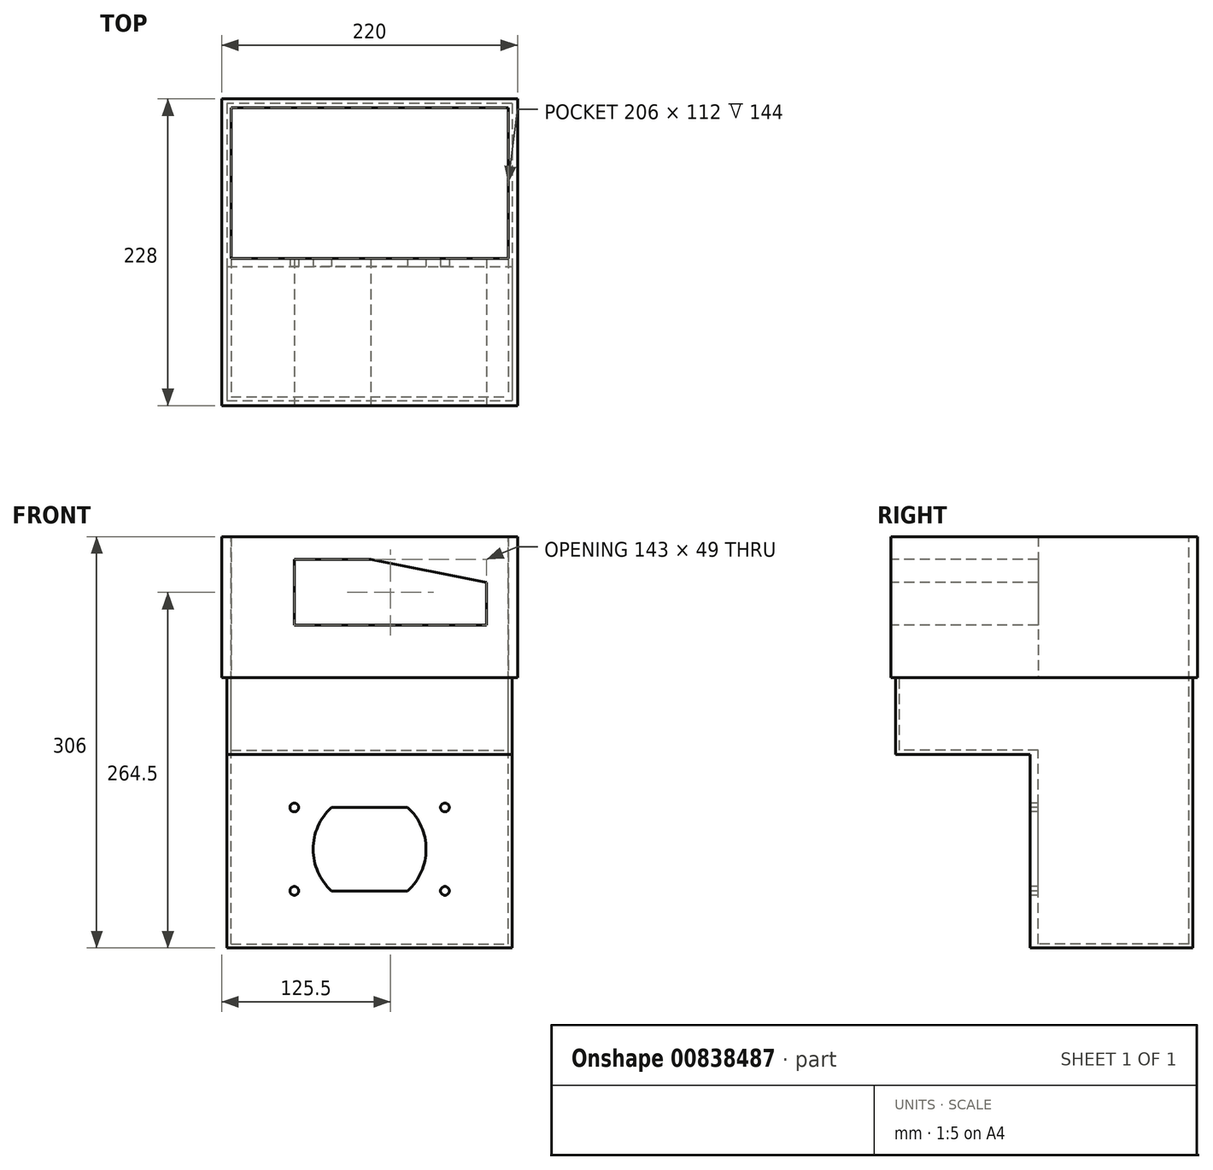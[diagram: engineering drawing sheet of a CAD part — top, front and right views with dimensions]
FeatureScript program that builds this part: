
annotation { "Feature Type Name" : "Feature", "Feature Type Description" : "" }
export const myFeature = defineFeature(function(context is Context, id is Id, definition is map)
    precondition{}
    {
        {
            var Q0;
            Q0=qCreatedBy(makeId("Top.planeOp"),FACE);
            var sketch = newSketch(context, id + "F0", { "sketchPlane" : qUnion([Q0])});
            skLineSegment(sketch, "E0.bottom", {"start": v(106, 110.5) * mm, "end": v(-106, 110.5) * mm});
            skLineSegment(sketch, "E0.top", {"start": v(106, -110.5) * mm, "end": v(-106, -110.5) * mm});
            skLineSegment(sketch, "E0.left", {"start": v(106, 110.5) * mm, "end": v(106, -110.5) * mm});
            skLineSegment(sketch, "E0.right", {"start": v(-106, 110.5) * mm, "end": v(-106, -110.5) * mm});
            skPoint(sketch, "E0.middle", {"position": v(0, 0) * mm});
            skSolve(sketch);
        }
        {
            var Q0;
            Q0=makeQuery(id+"F0.imprint","IMPRINT",FACE,{"disambiguationData":[TD([[makeQuery(id+"F0.imprint","IMPRINT",EDGE,{"derivedFrom":sQuery(id+"F0.wireOp",EDGE,"E0.bottom")}),1.0]])]});
            extrude(context, id + "F1", {"entities" : qUnion([Q0]), "depth" : 201 * mm, "offsetDistance" : 25 * mm});
        }
        {
            var Q0;
            Q0=makeQuery(id+"F1.opExtrude","CAP_FACE",FACE,{"disambiguationData":[OSD([sQuery(id+"F0.wireOp",EDGE,"E0.bottom"),sQuery(id+"F0.wireOp",EDGE,"E0.top"),sQuery(id+"F0.wireOp",EDGE,"E0.left"),sQuery(id+"F0.wireOp",EDGE,"E0.right")])],"isStart":false});
            var sketch = newSketch(context, id + "F2", { "sketchPlane" : qUnion([Q0])});
            skLineSegment(sketch, "E1.bottom", {"start": v(-103, 107.5) * mm, "end": v(103, 107.5) * mm});
            skLineSegment(sketch, "E1.top", {"start": v(-103, -4.5) * mm, "end": v(103, -4.5) * mm});
            skLineSegment(sketch, "E1.left", {"start": v(-103, 107.5) * mm, "end": v(-103, -7.5) * mm});
            skLineSegment(sketch, "E1.right", {"start": v(103, 107.5) * mm, "end": v(103, -7.5) * mm});
            skLineSegment(sketch, "E2", {"start": v(-103, -4.5) * mm, "end": v(-103, -107.5) * mm});
            skLineSegment(sketch, "E3", {"start": v(103, -4.5) * mm, "end": v(103, -107.5) * mm});
            skLineSegment(sketch, "E4", {"start": v(-103, -107.5) * mm, "end": v(103, -107.5) * mm});
            skLineSegment(sketch, "E5", {"start": v(-103, -7.5) * mm, "end": v(103, -7.5) * mm});
            skSolve(sketch);
        }
        {
            var Q0;
            Q0=makeQuery(id+"F2.imprint","IMPRINT",FACE,{"disambiguationData":[TD([[makeQuery(id+"F2.imprint","IMPRINT",EDGE,{"derivedFrom":sQuery(id+"F2.wireOp",EDGE,"E1.bottom")}),-1.0]])]});
            extrude(context, id + "F3", {"entities" : qUnion([Q0]), "operationType" : NewBodyOperationType.REMOVE, "oppositeDirection" : true, "depth" : 198 * mm, "offsetDistance" : 25 * mm});
        }
        {
            var Q0;
            Q0=makeQuery(id+"F1.opExtrude","SWEPT_FACE",FACE,{"disambiguationData":[OSD([sQuery(id+"F0.wireOp",EDGE,"E0.top")])]});
            var sketch = newSketch(context, id + "F4", { "sketchPlane" : qUnion([Q0])});
            skLineSegment(sketch, "E6.bottom", {"start": v(-106, 0) * mm, "end": v(106, 0) * mm});
            skLineSegment(sketch, "E6.top", {"start": v(-106, 144) * mm, "end": v(106, 144) * mm});
            skLineSegment(sketch, "E6.left", {"start": v(-106, 0) * mm, "end": v(-106, 144) * mm});
            skLineSegment(sketch, "E6.right", {"start": v(106, 0) * mm, "end": v(106, 144) * mm});
            skSolve(sketch);
        }
        {
            var Q0;
            Q0=makeQuery(id+"F4.imprint","IMPRINT",FACE,{"disambiguationData":[TD([[makeQuery(id+"F4.imprint","IMPRINT",EDGE,{"derivedFrom":sQuery(id+"F4.wireOp",EDGE,"E6.bottom")}),-1.0]])]});
            extrude(context, id + "F5", {"entities" : qUnion([Q0]), "operationType" : NewBodyOperationType.REMOVE, "oppositeDirection" : true, "depth" : 100 * mm, "offsetDistance" : 25 * mm});
        }
        {
            var Q0;
            Q0=makeQuery(id+"F2.imprint","IMPRINT",FACE,{"disambiguationData":[TD([[makeQuery(id+"F2.imprint","IMPRINT",EDGE,{"derivedFrom":sQuery(id+"F2.wireOp",EDGE,"E1.top")}),-1.0]])]});
            extrude(context, id + "F6", {"entities" : qUnion([Q0]), "operationType" : NewBodyOperationType.REMOVE, "oppositeDirection" : true, "depth" : 54 * mm, "offsetDistance" : 25 * mm});
        }
        {
            var Q0;
            {var subQ0=sQuery(id+"F2.wireOp",EDGE,"E4");Q0=makeQuery(id+"F2.imprint","IMPRINT",FACE,{"disambiguationData":[TD([[makeQuery(id+"F2.imprint","IMPRINT",EDGE,{"derivedFrom":subQ0}),1.0]])]});}
            extrude(context, id + "F7", {"entities" : qUnion([Q0]), "operationType" : NewBodyOperationType.REMOVE, "oppositeDirection" : true, "depth" : 54 * mm, "offsetDistance" : 25 * mm});
        }
        {
            var Q0;
            Q0=makeQuery(id+"F5.boolean.opBoolean","COPY",FACE,{"derivedFrom":makeQuery(id+"F5.opExtrude","CAP_FACE",FACE,{"disambiguationData":[OSD([sQuery(id+"F4.wireOp",EDGE,"E6.bottom"),sQuery(id+"F4.wireOp",EDGE,"E6.top"),sQuery(id+"F4.wireOp",EDGE,"E6.left"),sQuery(id+"F4.wireOp",EDGE,"E6.right")])],"isStart":false})});
            var sketch = newSketch(context, id + "F8", { "sketchPlane" : qUnion([Q0])});
            skLineSegment(sketch, "E7.bottom", {"start": v(34, 38) * mm, "end": v(-34, 38) * mm});
            skLineSegment(sketch, "E7.top", {"start": v(34, 109) * mm, "end": v(-34, 109) * mm});
            skPoint(sketch, "E7.middle", {"position": v(0, 73.5) * mm});
            skArc(sketch, "E8", {"start": v(27.78, 42) * mm, "mid": v(42, 73.5) * mm, "end": v(27.78, 105) * mm});
            skLineSegment(sketch, "E9.bottom", {"start": v(27.78, 42) * mm, "end": v(-27.78, 42) * mm});
            skLineSegment(sketch, "E9.top", {"start": v(27.78, 105) * mm, "end": v(-27.78, 105) * mm});
            skArc(sketch, "E10.trimOffspring", {"start": v(-27.78, 105) * mm, "mid": v(-42, 73.5) * mm, "end": v(-27.78, 42) * mm});
            skPoint(sketch, "E9.left.end.orphan", {"position": v(47.5, 105) * mm});
            skPoint(sketch, "E9.left.start.orphan", {"position": v(47.5, 42) * mm});
            skPoint(sketch, "E9.right.end.orphan", {"position": v(-47.5, 105) * mm});
            skPoint(sketch, "E9.right.start.orphan", {"position": v(-47.5, 42) * mm});
            skLineSegment(sketch, "E11.bottom", {"start": v(56, 42.5) * mm, "end": v(-56, 42.5) * mm});
            skLineSegment(sketch, "E11.top", {"start": v(56, 104.5) * mm, "end": v(-56, 104.5) * mm});
            skLineSegment(sketch, "E11.left", {"start": v(56, 42.5) * mm, "end": v(56, 104.5) * mm});
            skLineSegment(sketch, "E11.right", {"start": v(-56, 42.5) * mm, "end": v(-56, 104.5) * mm});
            skLineSegment(sketch, "E12", {"start": v(-55, 58.5) * mm, "end": v(-34, 38) * mm});
            skLineSegment(sketch, "E13", {"start": v(-55, 88.5) * mm, "end": v(-34, 109) * mm});
            skLineSegment(sketch, "E14", {"start": v(34, 38) * mm, "end": v(55, 58.5) * mm});
            skLineSegment(sketch, "E15", {"start": v(55, 88.5) * mm, "end": v(34, 109) * mm});
            skLineSegment(sketch, "E16.trimOffspring", {"start": v(55, 58.5) * mm, "end": v(55, 88.5) * mm});
            skPoint(sketch, "E7.left.start.orphan", {"position": v(55, 38) * mm});
            skPoint(sketch, "E17.orphan", {"position": v(55, 109) * mm});
            skLineSegment(sketch, "E18.trimOffspring", {"start": v(-55, 58.5) * mm, "end": v(-55, 88.5) * mm});
            skPoint(sketch, "E7.right.start.orphan", {"position": v(-55, 38) * mm});
            skPoint(sketch, "E19.trimOffspring.end.orphan", {"position": v(-55, 109) * mm});
            skCircle(sketch, "E20", {"center": v(-56, 42.5) * mm, "radius": 3.25 * mm});
            skCircle(sketch, "E21", {"center": v(-56, 104.5) * mm, "radius": 3.25 * mm});
            skCircle(sketch, "E22", {"center": v(56, 42.5) * mm, "radius": 3.25 * mm});
            skCircle(sketch, "E23", {"center": v(56, 104.5) * mm, "radius": 3.25 * mm});
            skSolve(sketch);
        }
        {
            var Q0;
            {var subQ0=sQuery(id+"F8.wireOp",EDGE,"E11.bottom");var subQ1=sQuery(id+"F8.wireOp",EDGE,"E8");var subQ2=makeQuery(id+"F8.imprint","INTERSECT",VERTEX,{"derivedFrom":[subQ1,subQ0]});Q0=makeQuery(id+"F8.imprint","IMPRINT",FACE,{"disambiguationData":[TD([[makeQuery(id+"F8.imprint","IMPRINT",EDGE,{"disambiguationData":[TD([[subQ2,-1.0]])],"derivedFrom":subQ1}),1.0]])]});}
            var Q1;
            {var subQ0=sQuery(id+"F8.wireOp",EDGE,"E11.left");var subQ1=sQuery(id+"F8.wireOp",EDGE,"E11.top");var subQ2=makeQuery(id+"F8.imprint","INTERSECT",VERTEX,{"derivedFrom":[subQ1,subQ0]});Q1=makeQuery(id+"F8.imprint","IMPRINT",FACE,{"disambiguationData":[TD([[makeQuery(id+"F8.imprint","IMPRINT",EDGE,{"disambiguationData":[TD([[subQ2,-1.0]])],"derivedFrom":subQ1}),-1.0]])]});}
            var Q2;
            {var subQ0=sQuery(id+"F8.wireOp",EDGE,"E11.left");var subQ1=sQuery(id+"F8.wireOp",EDGE,"E11.top");var subQ2=makeQuery(id+"F8.imprint","INTERSECT",VERTEX,{"derivedFrom":[subQ1,subQ0]});Q2=makeQuery(id+"F8.imprint","IMPRINT",FACE,{"disambiguationData":[TD([[makeQuery(id+"F8.imprint","IMPRINT",EDGE,{"disambiguationData":[TD([[subQ2,-1.0]])],"derivedFrom":subQ1}),1.0]])]});}
            var Q3;
            {var subQ0=sQuery(id+"F8.wireOp",EDGE,"E11.left");var subQ1=sQuery(id+"F8.wireOp",EDGE,"E11.bottom");var subQ2=makeQuery(id+"F8.imprint","INTERSECT",VERTEX,{"derivedFrom":[subQ1,subQ0]});Q3=makeQuery(id+"F8.imprint","IMPRINT",FACE,{"disambiguationData":[TD([[makeQuery(id+"F8.imprint","IMPRINT",EDGE,{"disambiguationData":[TD([[subQ2,-1.0]])],"derivedFrom":subQ1}),-1.0]])]});}
            var Q4;
            {var subQ0=sQuery(id+"F8.wireOp",EDGE,"E11.left");var subQ1=sQuery(id+"F8.wireOp",EDGE,"E11.bottom");var subQ2=makeQuery(id+"F8.imprint","INTERSECT",VERTEX,{"derivedFrom":[subQ1,subQ0]});Q4=makeQuery(id+"F8.imprint","IMPRINT",FACE,{"disambiguationData":[TD([[makeQuery(id+"F8.imprint","IMPRINT",EDGE,{"disambiguationData":[TD([[subQ2,-1.0]])],"derivedFrom":subQ1}),1.0]])]});}
            var Q5;
            {var subQ0=sQuery(id+"F8.wireOp",EDGE,"E11.right");var subQ1=sQuery(id+"F8.wireOp",EDGE,"E11.bottom");var subQ2=makeQuery(id+"F8.imprint","INTERSECT",VERTEX,{"derivedFrom":[subQ1,subQ0]});Q5=makeQuery(id+"F8.imprint","IMPRINT",FACE,{"disambiguationData":[TD([[makeQuery(id+"F8.imprint","IMPRINT",EDGE,{"disambiguationData":[TD([[subQ2,1.0]])],"derivedFrom":subQ1}),1.0]])]});}
            var Q6;
            {var subQ0=sQuery(id+"F8.wireOp",EDGE,"E11.right");var subQ1=sQuery(id+"F8.wireOp",EDGE,"E11.bottom");var subQ2=makeQuery(id+"F8.imprint","INTERSECT",VERTEX,{"derivedFrom":[subQ1,subQ0]});Q6=makeQuery(id+"F8.imprint","IMPRINT",FACE,{"disambiguationData":[TD([[makeQuery(id+"F8.imprint","IMPRINT",EDGE,{"disambiguationData":[TD([[subQ2,1.0]])],"derivedFrom":subQ1}),-1.0]])]});}
            var Q7;
            {var subQ0=sQuery(id+"F8.wireOp",EDGE,"E11.right");var subQ1=sQuery(id+"F8.wireOp",EDGE,"E11.top");var subQ2=makeQuery(id+"F8.imprint","INTERSECT",VERTEX,{"derivedFrom":[subQ1,subQ0]});Q7=makeQuery(id+"F8.imprint","IMPRINT",FACE,{"disambiguationData":[TD([[makeQuery(id+"F8.imprint","IMPRINT",EDGE,{"disambiguationData":[TD([[subQ2,1.0]])],"derivedFrom":subQ1}),1.0]])]});}
            var Q8;
            {var subQ0=sQuery(id+"F8.wireOp",EDGE,"E11.right");var subQ1=sQuery(id+"F8.wireOp",EDGE,"E11.top");var subQ2=makeQuery(id+"F8.imprint","INTERSECT",VERTEX,{"derivedFrom":[subQ1,subQ0]});Q8=makeQuery(id+"F8.imprint","IMPRINT",FACE,{"disambiguationData":[TD([[makeQuery(id+"F8.imprint","IMPRINT",EDGE,{"disambiguationData":[TD([[subQ2,1.0]])],"derivedFrom":subQ1}),-1.0]])]});}
            extrude(context, id + "F9", {"entities" : qUnion([Q0, Q1, Q2, Q3, Q4, Q5, Q6, Q7, Q8]), "operationType" : NewBodyOperationType.REMOVE, "endBound" : BoundingType.UP_TO_NEXT, "oppositeDirection" : true, "depth" : 25 * mm, "offsetDistance" : 25 * mm});
        }
        {
            var Q0;
            Q0=makeQuery(id+"F3.boolean.opBoolean","COPY",FACE,{"derivedFrom":makeQuery(id+"F3.opExtrude","CAP_FACE",FACE,{"disambiguationData":[OSD([sQuery(id+"F2.wireOp",EDGE,"E1.bottom"),sQuery(id+"F2.wireOp",EDGE,"E1.top"),sQuery(id+"F2.wireOp",EDGE,"E1.left"),sQuery(id+"F2.wireOp",EDGE,"E1.right")])],"isStart":false})});
            var sketch = newSketch(context, id + "F10", { "sketchPlane" : qUnion([Q0])});
            skLineSegment(sketch, "E24.bottom", {"start": v(110, 114) * mm, "end": v(-110, 114) * mm});
            skLineSegment(sketch, "E24.top", {"start": v(110, -114) * mm, "end": v(-110, -114) * mm});
            skLineSegment(sketch, "E24.left", {"start": v(110, 114) * mm, "end": v(110, -114) * mm});
            skLineSegment(sketch, "E24.right", {"start": v(-110, 114) * mm, "end": v(-110, -114) * mm});
            skPoint(sketch, "E24.middle", {"position": v(0, 0) * mm});
            skSolve(sketch);
        }
        {
            var Q0;
            Q0=makeQuery(id+"F10.imprint","IMPRINT",FACE,{"disambiguationData":[TD([[makeQuery(id+"F10.imprint","IMPRINT",EDGE,{"derivedFrom":sQuery(id+"F10.wireOp",EDGE,"E24.bottom")}),1.0]])]});
            extrude(context, id + "F11", {"entities" : qUnion([Q0]), "operationType" : NewBodyOperationType.ADD, "depth" : 303 * mm, "offsetDistance" : 25 * mm, "hasSecondDirection" : true, "secondDirectionOppositeDirection" : false, "secondDirectionDepth" : 198 * mm});
        }
        {
            var Q0;
            Q0=makeQuery(id+"F11.opExtrude","SWEPT_FACE",FACE,{"disambiguationData":[OSD([sQuery(id+"F10.wireOp",EDGE,"E24.top")])]});
            var sketch = newSketch(context, id + "F12", { "sketchPlane" : qUnion([Q0])});
            skSolve(sketch);
        }
        {
            var Q0;
            {var subQ0=sQuery(id+"F10.wireOp",EDGE,"E24.top");Q0=makeQuery(id+"F12.imprint","IMPRINT",FACE,{"disambiguationData":[TD([[makeQuery(id+"F12.imprint","IMPRINT",EDGE,{"derivedFrom":makeQuery(id+"F11.opExtrude","CAP_EDGE",EDGE,{"disambiguationData":[OSD([subQ0])],"isStart":true})}),-1.0]])]});}
            var sketch = newSketch(context, id + "F13", { "sketchPlane" : qUnion([Q0])});
            skLineSegment(sketch, "E25.bottom", {"start": v(-56, 289) * mm, "end": v(1, 289) * mm});
            skLineSegment(sketch, "E25.top", {"start": v(-56, 240) * mm, "end": v(87, 240) * mm});
            skLineSegment(sketch, "E25.left", {"start": v(-56, 289) * mm, "end": v(-56, 240) * mm});
            skLineSegment(sketch, "E26", {"start": v(1, 289) * mm, "end": v(87, 272) * mm});
            skLineSegment(sketch, "E27", {"start": v(87, 272) * mm, "end": v(87, 240) * mm});
            skSolve(sketch);
        }
        {
            var Q0;
            Q0=makeQuery(id+"F13.imprint","IMPRINT",FACE,{"disambiguationData":[TD([[makeQuery(id+"F13.imprint","IMPRINT",EDGE,{"derivedFrom":sQuery(id+"F13.wireOp",EDGE,"E25.bottom")}),-1.0]])]});
            extrude(context, id + "F14", {"entities" : qUnion([Q0]), "operationType" : NewBodyOperationType.REMOVE, "endBound" : BoundingType.UP_TO_NEXT, "oppositeDirection" : true, "depth" : 25 * mm, "offsetDistance" : 25 * mm});
        }
    });
